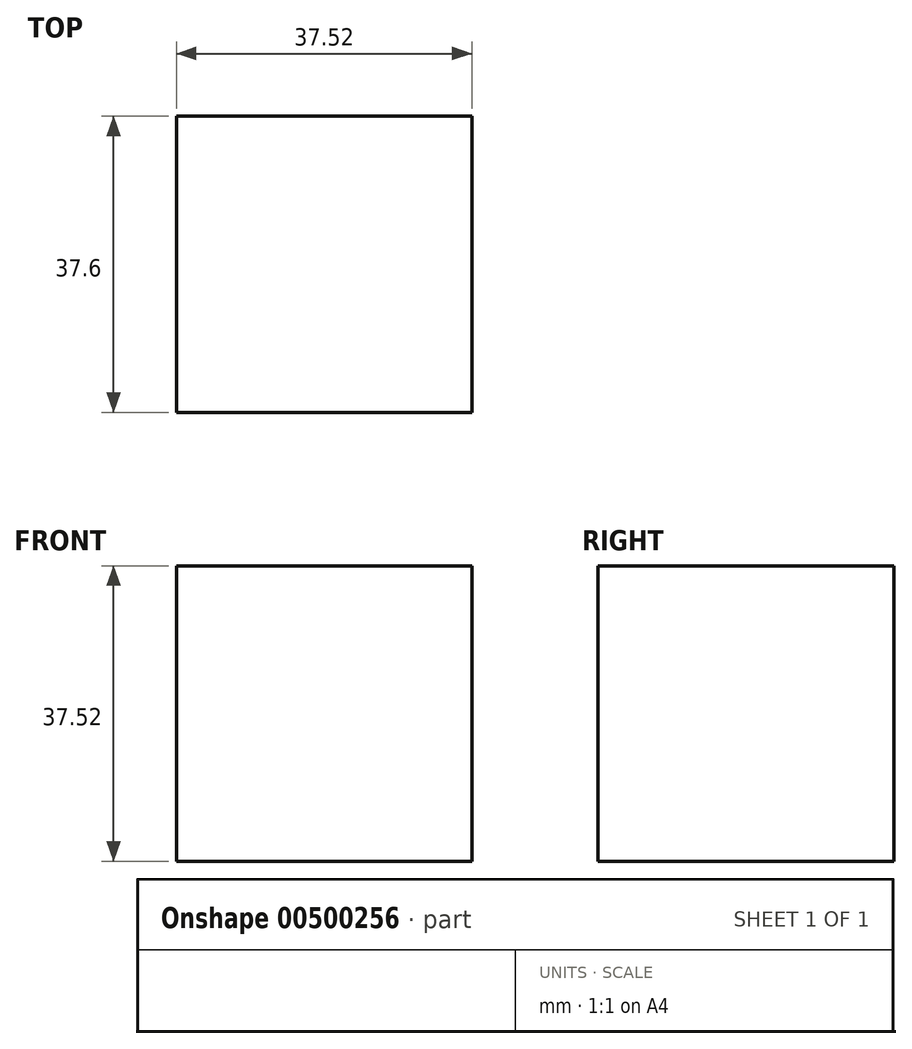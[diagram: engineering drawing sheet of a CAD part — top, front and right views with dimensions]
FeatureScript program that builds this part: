
annotation { "Feature Type Name" : "Feature", "Feature Type Description" : "" }
export const myFeature = defineFeature(function(context is Context, id is Id, definition is map)
    precondition{}
    {
        {
            var Q0;
            Q0=qCreatedBy(makeId("Front.planeOp"),FACE);
            var sketch = newSketch(context, id + "F0", { "sketchPlane" : qUnion([Q0])});
            skCircle(sketch, "E0.cCircle", {"center": v(0, 0) * mm, "radius": 26.53 * mm, "construction": true});
            skLineSegment(sketch, "E0.0", {"start": v(18.76, -18.76) * mm, "end": v(-18.76, -18.76) * mm});
            skLineSegment(sketch, "E0.1", {"start": v(-18.76, -18.76) * mm, "end": v(-18.76, 18.76) * mm});
            skLineSegment(sketch, "E0.2", {"start": v(-18.76, 18.76) * mm, "end": v(18.76, 18.76) * mm});
            skLineSegment(sketch, "E0.3", {"start": v(18.76, 18.76) * mm, "end": v(18.76, -18.76) * mm});
            skSolve(sketch);
        }
        {
            var Q0;
            Q0=makeQuery(id+"F0.imprint","IMPRINT",FACE,{"disambiguationData":[TD([[makeQuery(id+"F0.imprint","IMPRINT",EDGE,{"derivedFrom":sQuery(id+"F0.wireOp",EDGE,"E0.0")}),-1.0]])]});
            extrude(context, id + "F1", {"entities" : qUnion([Q0]), "depth" : 37.6 * mm});
        }
    });
